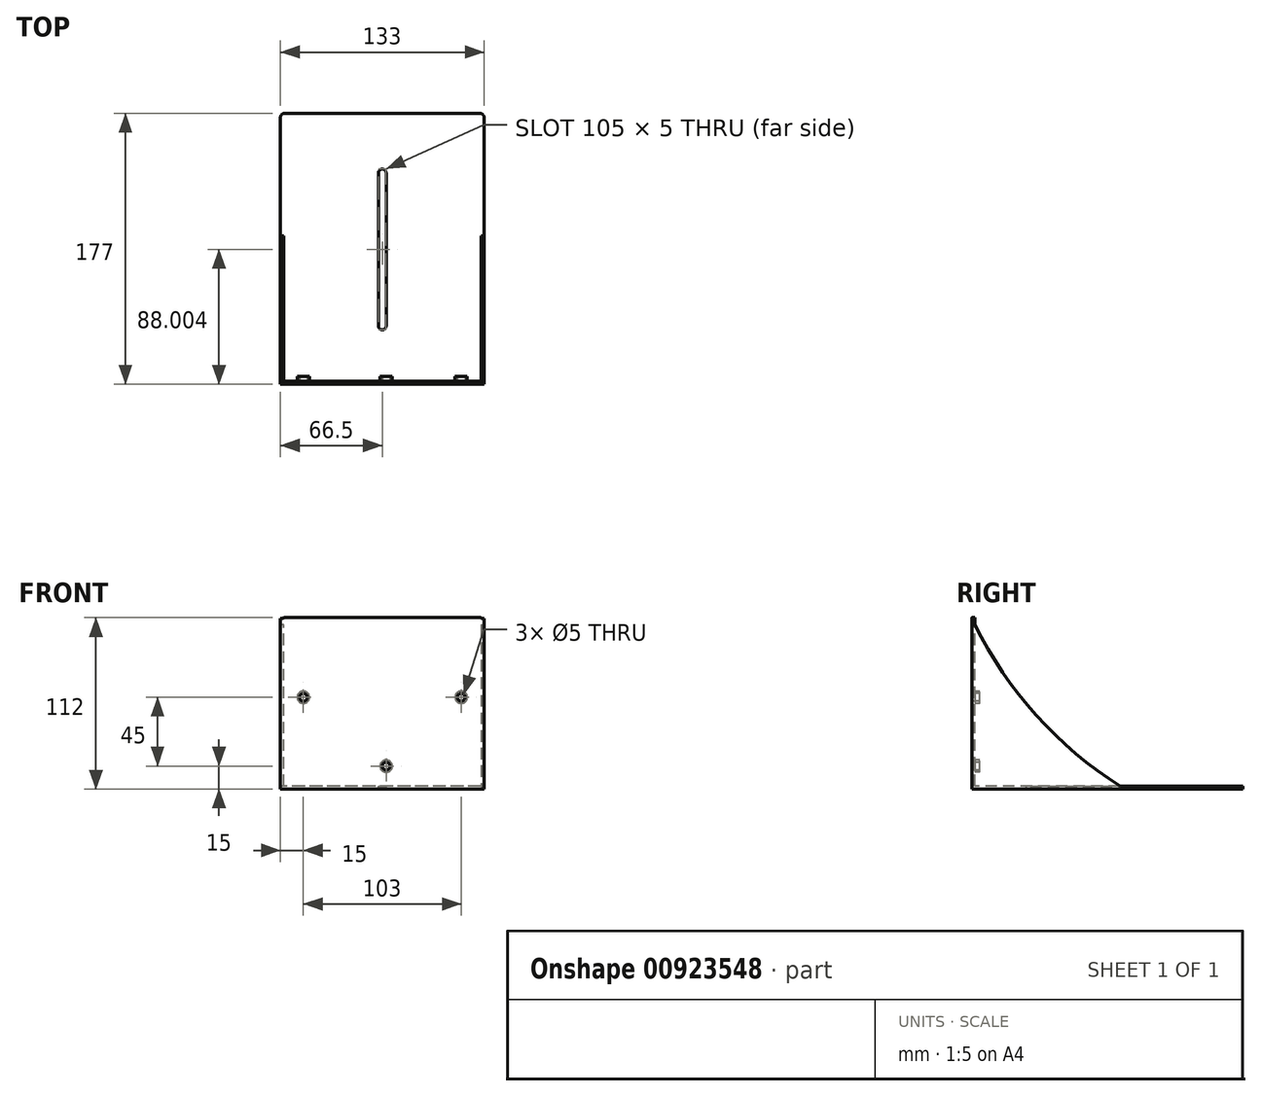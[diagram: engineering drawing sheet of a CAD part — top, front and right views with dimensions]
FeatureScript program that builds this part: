
annotation { "Feature Type Name" : "Feature", "Feature Type Description" : "" }
export const myFeature = defineFeature(function(context is Context, id is Id, definition is map)
    precondition{}
    {
        {
            var Q0;
            Q0=qCreatedBy(makeId("Right.planeOp"),FACE);
            var sketch = newSketch(context, id + "F0", { "sketchPlane" : qUnion([Q0])});
            skLineSegment(sketch, "E0", {"start": v(-128.96, 110) * mm, "end": v(-128.96, 0) * mm});
            skLineSegment(sketch, "E1", {"start": v(-128.96, 0) * mm, "end": v(46.04, 0) * mm});
            skLineSegment(sketch, "E2.0", {"start": v(-130.96, 110) * mm, "end": v(-130.96, 0) * mm});
            skLineSegment(sketch, "E3.0", {"start": v(-130.96, -2) * mm, "end": v(46.04, -2) * mm});
            skLineSegment(sketch, "E4", {"start": v(-130.96, 110) * mm, "end": v(-128.96, 110) * mm});
            skLineSegment(sketch, "E5", {"start": v(46.04, -2) * mm, "end": v(46.04, 0) * mm});
            skLineSegment(sketch, "E6", {"start": v(-130.96, 0) * mm, "end": v(-130.96, -2) * mm});
            skSolve(sketch);
        }
        {
            var Q0;
            Q0 = qSketchRegion(id + "F0", true);
            extrude(context, id + "F1", {"entities" : qUnion([Q0]), "depth" : 133 * mm, "offsetDistance" : 25 * mm});
        }
        {
            var Q0;
            Q0=makeQuery(id+"F1.opExtrude","SWEPT_FACE",FACE,{"disambiguationData":[OSD([sQuery(id+"F0.wireOp",EDGE,"E2.0"),sQuery(id+"F0.wireOp",EDGE,"E6")])]});
            var sketch = newSketch(context, id + "F2", { "sketchPlane" : qUnion([Q0])});
            skCircle(sketch, "E7", {"center": v(69, 13) * mm, "radius": 2.5 * mm});
            skCircle(sketch, "E8", {"center": v(15, 58) * mm, "radius": 2.5 * mm});
            skCircle(sketch, "E9", {"center": v(118, 58) * mm, "radius": 2.5 * mm});
            skSolve(sketch);
        }
        {
            var Q0;
            Q0 = qSketchRegion(id + "F2", true);
            extrude(context, id + "F3", {"entities" : qUnion([Q0]), "operationType" : NewBodyOperationType.REMOVE, "oppositeDirection" : true, "depth" : 25 * mm, "offsetDistance" : 25 * mm});
        }
        {
            var Q0;
            Q0=makeQuery(id+"F1.opExtrude","SWEPT_FACE",FACE,{"disambiguationData":[OSD([sQuery(id+"F0.wireOp",EDGE,"E2.0"),sQuery(id+"F0.wireOp",EDGE,"E6")])]});
            var sketch = newSketch(context, id + "F4", { "sketchPlane" : qUnion([Q0])});
            skCircle(sketch, "E10", {"center": v(15, 58) * mm, "radius": 4 * mm});
            skCircle(sketch, "E11", {"center": v(69, 13) * mm, "radius": 4 * mm});
            skCircle(sketch, "E12", {"center": v(118, 58) * mm, "radius": 4 * mm});
            skSolve(sketch);
        }
        {
            var Q0;
            Q0 = qSketchRegion(id + "F4", true);
            extrude(context, id + "F5", {"entities" : qUnion([Q0]), "operationType" : NewBodyOperationType.ADD, "oppositeDirection" : true, "depth" : 5 * mm, "offsetDistance" : 25 * mm});
        }
        {
            var Q0;
            Q0 = qSketchRegion(id + "F2", true);
            extrude(context, id + "F6", {"entities" : qUnion([Q0]), "operationType" : NewBodyOperationType.REMOVE, "oppositeDirection" : true, "depth" : 25 * mm, "offsetDistance" : 25 * mm});
        }
        {
            var Q0;
            Q0=makeQuery(id+"F1.opExtrude","CAP_EDGE",EDGE,{"disambiguationData":[OSD([sQuery(id+"F0.wireOp",EDGE,"E4")])],"isStart":true});
            var Q1;
            Q1=makeQuery(id+"F1.opExtrude","CAP_EDGE",EDGE,{"disambiguationData":[OSD([sQuery(id+"F0.wireOp",EDGE,"E4")])],"isStart":false});
            var Q2;
            Q2=makeQuery(id+"F1.opExtrude","CAP_EDGE",EDGE,{"disambiguationData":[OSD([sQuery(id+"F0.wireOp",EDGE,"E5")])],"isStart":false});
            var Q3;
            Q3=makeQuery(id+"F1.opExtrude","CAP_EDGE",EDGE,{"disambiguationData":[OSD([sQuery(id+"F0.wireOp",EDGE,"E5")])],"isStart":true});
            fillet(context, id + "F7", {"entities" : qUnion([Q0, Q1, Q2, Q3]), "radius" : 3 * mm, "tangentPropagation" : true, "allowEdgeOverflow" : false});
        }
        {
            var Q0;
            Q0=makeQuery(id+"F1.opExtrude","SWEPT_FACE",FACE,{"disambiguationData":[OSD([sQuery(id+"F0.wireOp",EDGE,"E1")])]});
            var sketch = newSketch(context, id + "F8", { "sketchPlane" : qUnion([Q0])});
            skLineSegment(sketch, "E13.left", {"start": v(64, -92.96) * mm, "end": v(64, 7.04) * mm});
            skLineSegment(sketch, "E13.right", {"start": v(69, -92.96) * mm, "end": v(69, 7.04) * mm});
            skPoint(sketch, "E13.middle", {"position": v(66.5, -42.96) * mm});
            skPoint(sketch, "E13.middle.positionSnap0", {"position": v(0, -42.96) * mm});
            skPoint(sketch, "E13.centerSnap0", {"position": v(0, -42.96) * mm});
            skArc(sketch, "E14", {"start": v(69, 7.04) * mm, "mid": v(66.5, 9.54) * mm, "end": v(64, 7.04) * mm});
            skArc(sketch, "E15", {"start": v(64, -92.96) * mm, "mid": v(66.5, -95.46) * mm, "end": v(69, -92.96) * mm});
            skSolve(sketch);
        }
        {
            var Q0;
            Q0 = qSketchRegion(id + "F8", true);
            extrude(context, id + "F9", {"entities" : qUnion([Q0]), "operationType" : NewBodyOperationType.REMOVE, "oppositeDirection" : true, "depth" : 25 * mm, "offsetDistance" : 25 * mm});
        }
        {
            var Q0;
            Q0=makeQuery(id+"F1.opExtrude","CAP_FACE",FACE,{"disambiguationData":[OSD([sQuery(id+"F0.wireOp",EDGE,"E0"),sQuery(id+"F0.wireOp",EDGE,"E1"),sQuery(id+"F0.wireOp",EDGE,"E2.0"),sQuery(id+"F0.wireOp",EDGE,"E3.0"),sQuery(id+"F0.wireOp",EDGE,"E4"),sQuery(id+"F0.wireOp",EDGE,"E5"),sQuery(id+"F0.wireOp",EDGE,"E6")])],"isStart":false});
            var sketch = newSketch(context, id + "F10", { "sketchPlane" : qUnion([Q0])});
            skLineSegment(sketch, "E16.bottom", {"start": v(-130.96, -2) * mm, "end": v(-30.96, -2) * mm});
            skLineSegment(sketch, "E16.left", {"start": v(-130.96, -2) * mm, "end": v(-130.96, 109.6) * mm});
            skArc(sketch, "E17", {"start": v(-130.96, 109.6) * mm, "mid": v(-89.17, 46.44) * mm, "end": v(-30.96, -2) * mm});
            skSolve(sketch);
        }
        {
            var Q0;
            Q0 = qSketchRegion(id + "F10", true);
            extrude(context, id + "F11", {"entities" : qUnion([Q0]), "operationType" : NewBodyOperationType.ADD, "oppositeDirection" : true, "depth" : 2 * mm, "offsetDistance" : 25 * mm});
        }
        {
            var Q0;
            Q0=makeQuery(id+"F1.opExtrude","CAP_FACE",FACE,{"disambiguationData":[OSD([sQuery(id+"F0.wireOp",EDGE,"E0"),sQuery(id+"F0.wireOp",EDGE,"E1"),sQuery(id+"F0.wireOp",EDGE,"E2.0"),sQuery(id+"F0.wireOp",EDGE,"E3.0"),sQuery(id+"F0.wireOp",EDGE,"E4"),sQuery(id+"F0.wireOp",EDGE,"E5"),sQuery(id+"F0.wireOp",EDGE,"E6")])],"isStart":true});
            var sketch = newSketch(context, id + "F12", { "sketchPlane" : qUnion([Q0])});
            skLineSegment(sketch, "E18.bottom", {"start": v(130.96, -2) * mm, "end": v(30.96, -2) * mm});
            skLineSegment(sketch, "E18.left", {"start": v(130.96, -2) * mm, "end": v(130.96, 109.6) * mm});
            skArc(sketch, "E19", {"start": v(30.96, -2) * mm, "mid": v(89.17, 46.44) * mm, "end": v(130.96, 109.6) * mm});
            skSolve(sketch);
        }
        {
            var Q0;
            Q0 = qSketchRegion(id + "F12", true);
            extrude(context, id + "F13", {"entities" : qUnion([Q0]), "operationType" : NewBodyOperationType.ADD, "oppositeDirection" : true, "depth" : 2 * mm, "offsetDistance" : 25 * mm});
        }
    });
